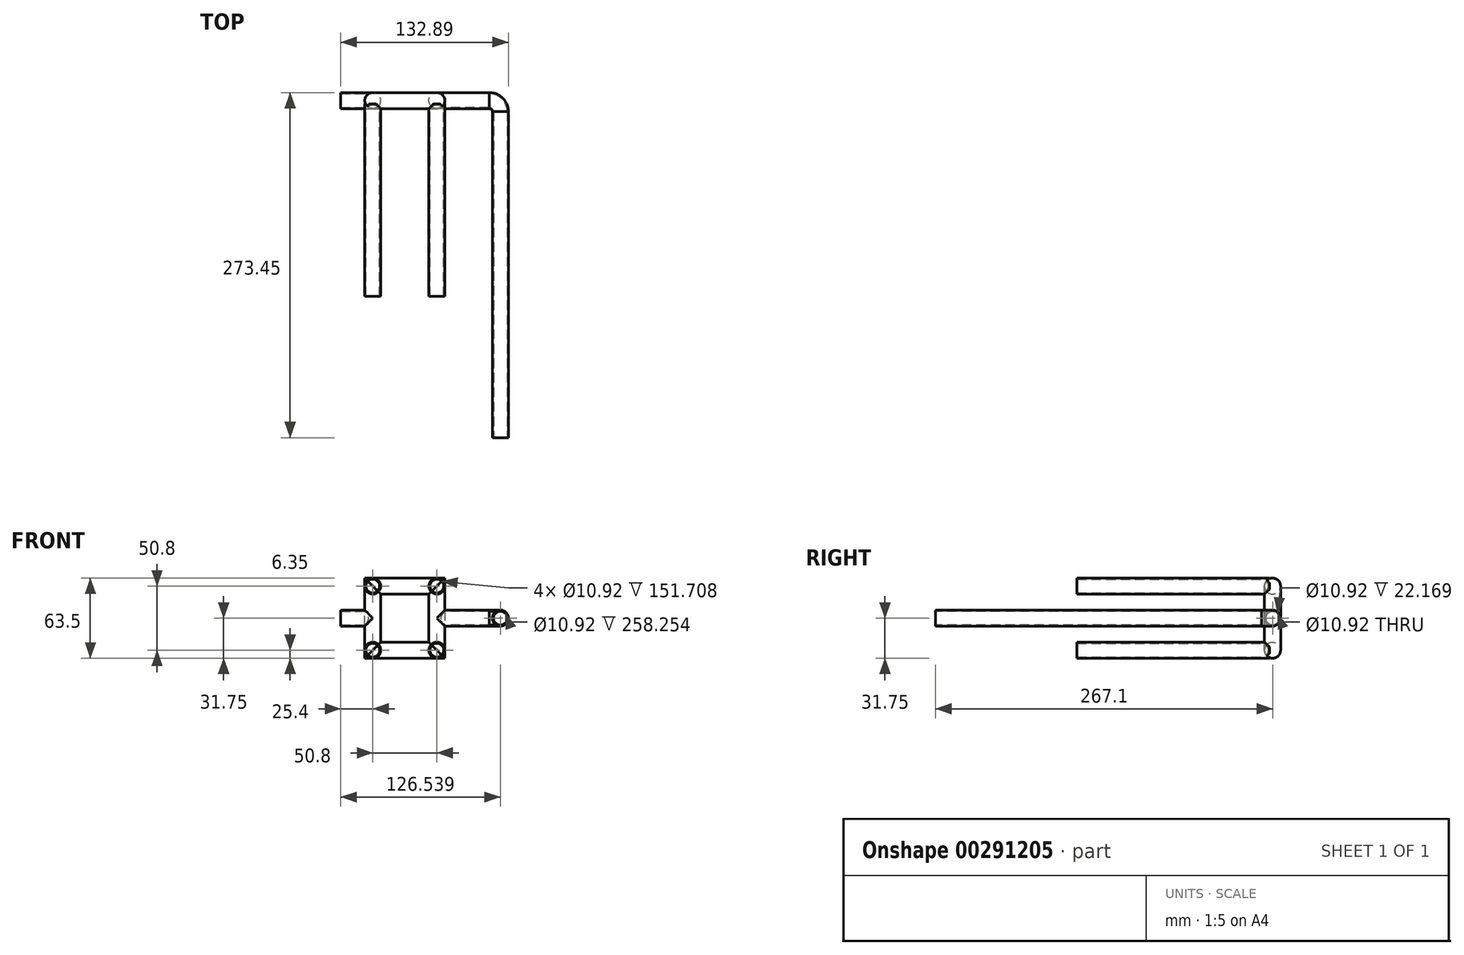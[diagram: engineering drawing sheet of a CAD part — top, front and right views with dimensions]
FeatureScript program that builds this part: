
annotation { "Feature Type Name" : "Feature", "Feature Type Description" : "" }
export const myFeature = defineFeature(function(context is Context, id is Id, definition is map)
    precondition{}
    {
        {
            var Q0;
            Q0=qCreatedBy(makeId("Front.planeOp"),FACE);
            var sketch = newSketch(context, id + "F0", { "sketchPlane" : qUnion([Q0])});
            skLineSegment(sketch, "E0", {"start": v(-31.75, 31.75) * mm, "end": v(31.75, 31.75) * mm});
            skLineSegment(sketch, "E1", {"start": v(31.75, 31.75) * mm, "end": v(31.75, -31.75) * mm});
            skLineSegment(sketch, "E2", {"start": v(31.75, -31.75) * mm, "end": v(-31.75, -31.75) * mm});
            skLineSegment(sketch, "E3", {"start": v(-31.75, 31.75) * mm, "end": v(-31.75, -31.75) * mm});
            skLineSegment(sketch, "E4.0", {"start": v(25.4, 25.4) * mm, "end": v(25.4, -25.4) * mm});
            skLineSegment(sketch, "E4.1", {"start": v(-25.4, 25.4) * mm, "end": v(25.4, 25.4) * mm});
            skLineSegment(sketch, "E4.2", {"start": v(-25.4, 25.4) * mm, "end": v(-25.4, -25.4) * mm});
            skLineSegment(sketch, "E4.3", {"start": v(25.4, -25.4) * mm, "end": v(-25.4, -25.4) * mm});
            skSolve(sketch);
        }
        {
            var Q0;
            Q0=qCreatedBy(makeId("Right.planeOp"),FACE);
            var sketch = newSketch(context, id + "F1", { "sketchPlane" : qUnion([Q0])});
            skCircle(sketch, "E5", {"center": v(0, 25.4) * mm, "radius": 6.35 * mm});
            skSolve(sketch);
        }
        {
            var Q0;
            Q0=makeQuery(id+"F1.imprint","IMPRINT",FACE,{"disambiguationData":[TD([[makeQuery(id+"F1.imprint","IMPRINT",EDGE,{"derivedFrom":sQuery(id+"F1.wireOp",EDGE,"E5")}),1.0]])]});
            var Q1;
            Q1=sQuery(id+"F0.wireOp",EDGE,"E4.0");
            var Q2;
            Q2=sQuery(id+"F0.wireOp",EDGE,"E4.3");
            var Q3;
            Q3=sQuery(id+"F0.wireOp",EDGE,"E4.2");
            var Q4;
            Q4=sQuery(id+"F0.wireOp",EDGE,"E4.1");
            sweep(context, id + "F2", {"profiles" : qUnion([Q0]), "path" : qUnion([Q1, Q2, Q3, Q4])});
        }
        {
            var Q0;
            Q0=qCreatedBy(makeId("Front.planeOp"),FACE);
            cPlane(context, id + "F3", {"entities" : qUnion([Q0]), "cplaneType" : CPlaneType.OFFSET, "offset" : 2.54 * mm, "width" : 152.4 * mm, "height" : 152.4 * mm});
        }
        {
            var Q0;
            Q0=qCreatedBy(id+"F3.planeOp",FACE);
            var sketch = newSketch(context, id + "F4", { "sketchPlane" : qUnion([Q0])});
            skCircle(sketch, "E6", {"center": v(25.4, 25.4) * mm, "radius": 6.35 * mm});
            skCircle(sketch, "E7", {"center": v(-25.4, 25.4) * mm, "radius": 6.35 * mm});
            skCircle(sketch, "E8", {"center": v(-25.4, -25.4) * mm, "radius": 6.35 * mm});
            skCircle(sketch, "E9", {"center": v(25.4, -25.4) * mm, "radius": 6.35 * mm});
            skCircle(sketch, "E10", {"center": v(25.4, 25.4) * mm, "radius": 5.46 * mm});
            skCircle(sketch, "E11", {"center": v(-25.4, 25.4) * mm, "radius": 5.46 * mm});
            skCircle(sketch, "E12", {"center": v(-25.4, -25.4) * mm, "radius": 5.46 * mm});
            skCircle(sketch, "E13", {"center": v(25.4, -25.4) * mm, "radius": 5.46 * mm});
            skSolve(sketch);
        }
        {
            var Q0;
            Q0 = qSketchRegion(id + "F4", true);
            extrude(context, id + "F5", {"entities" : qUnion([Q0]), "operationType" : NewBodyOperationType.ADD, "depth" : 152.4 * mm});
        }
        {
            var Q0;
            Q0=qCreatedBy(makeId("Right.planeOp"),FACE);
            cPlane(context, id + "F6", {"entities" : qUnion([Q0]), "cplaneType" : CPlaneType.OFFSET, "offset" : 25.4 * mm, "width" : 152.4 * mm, "height" : 152.4 * mm});
        }
        {
            var Q0;
            Q0=qCreatedBy(id+"F6.planeOp",FACE);
            var sketch = newSketch(context, id + "F7", { "sketchPlane" : qUnion([Q0])});
            skCircle(sketch, "E14", {"center": v(0, 0) * mm, "radius": 6.35 * mm});
            skCircle(sketch, "E15", {"center": v(0, 0) * mm, "radius": 5.46 * mm});
            skSolve(sketch);
        }
        {
            var Q0;
            Q0 = qSketchRegion(id + "F7", true);
            extrude(context, id + "F8", {"entities" : qUnion([Q0]), "operationType" : NewBodyOperationType.ADD, "depth" : 25.4 * mm});
        }
        {
            var Q0;
            Q0=qCreatedBy(makeId("Right.planeOp"),FACE);
            cPlane(context, id + "F9", {"entities" : qUnion([Q0]), "cplaneType" : CPlaneType.OFFSET, "offset" : 25.4 * mm, "oppositeDirection" : true, "width" : 152.4 * mm, "height" : 152.4 * mm});
        }
        {
            var Q0;
            Q0=qCreatedBy(id+"F9.planeOp",FACE);
            var sketch = newSketch(context, id + "F10", { "sketchPlane" : qUnion([Q0])});
            skCircle(sketch, "E16", {"center": v(0, 0) * mm, "radius": 6.35 * mm});
            skCircle(sketch, "E17", {"center": v(0, 0) * mm, "radius": 5.46 * mm});
            skSolve(sketch);
        }
        {
            var Q0;
            Q0 = qSketchRegion(id + "F10", true);
            extrude(context, id + "F11", {"entities" : qUnion([Q0]), "operationType" : NewBodyOperationType.ADD, "oppositeDirection" : true, "depth" : 25.4 * mm});
        }
        {
            var Q0;
            Q0=makeQuery(id+"F8.opExtrude","CAP_FACE",FACE,{"disambiguationData":[OSD([sQuery(id+"F7.wireOp",EDGE,"E14"),sQuery(id+"F7.wireOp",EDGE,"E15")])],"isStart":false});
            var sketch = newSketch(context, id + "F12", { "sketchPlane" : qUnion([Q0])});
            skCircle(sketch, "E18", {"center": v(0, 0) * mm, "radius": 6.35 * mm});
            skCircle(sketch, "E19", {"center": v(0, 0) * mm, "radius": 5.46 * mm});
            skSolve(sketch);
        }
        {
            var Q0;
            Q0=qCreatedBy(makeId("Top.planeOp"),FACE);
            var sketch = newSketch(context, id + "F13", { "sketchPlane" : qUnion([Q0])});
            skLineSegment(sketch, "E20", {"start": v(50.85, 0) * mm, "end": v(66.85, 0) * mm});
            skLineSegment(sketch, "E21", {"start": v(75.74, -8.9) * mm, "end": v(75.74, -267.14) * mm});
            skPoint(sketch, "E22.visualSharp", {"position": v(75.74, 0) * mm});
            skArc(sketch, "E22.filletArc", {"start": v(75.74, -8.89) * mm, "mid": v(73.13, -2.6) * mm, "end": v(66.85, 0) * mm});
            skLineSegment(sketch, "E23.MirrorCS", {"start": v(-50.85, 0) * mm, "end": v(-66.85, 0) * mm});
            skArc(sketch, "E24.MirrorCS", {"start": v(-75.74, -8.89) * mm, "mid": v(-73.13, -2.6) * mm, "end": v(-66.85, 0) * mm});
            skLineSegment(sketch, "E25.MirrorCS", {"start": v(-75.74, -8.9) * mm, "end": v(-75.74, -267.14) * mm});
            skSolve(sketch);
        }
        {
            var Q0;
            Q0=makeQuery(id+"F12.imprint","IMPRINT",FACE,{"disambiguationData":[TD([[makeQuery(id+"F12.imprint","IMPRINT",EDGE,{"derivedFrom":sQuery(id+"F12.wireOp",EDGE,"E18")}),1.0]])]});
            var Q1;
            Q1=sQuery(id+"F13.wireOp",EDGE,"E20");
            var Q2;
            Q2=sQuery(id+"F13.wireOp",EDGE,"E21");
            var Q3;
            Q3=sQuery(id+"F13.wireOp",EDGE,"E22.filletArc");
            sweep(context, id + "F14", {"operationType" : NewBodyOperationType.ADD, "profiles" : qUnion([Q0]), "path" : qUnion([Q1, Q2, Q3])});
        }
    });
